# Revit family: Lighting_Ceiling-Mounted_Nordlux_Kaito-dim-LED
name_source: partatom
category: Lighting Fixtures
revit_build: Autodesk Revit 2018 (Build: 20170223_1515(x64)
units: mm (PartAtom-declared; Revit-internal decimal feet)

## family parameters
Cut with Voids When Loaded = No
Host = Face
Light Source = No
OmniClass Number = 23.35.47.11
OmniClass Title = Lighting Fixtures
Part Type = Normal
Room Calculation Point = No
Round Connector Dimension = Use Diameter
Shared = No

## types (2) — shared parameters
Apparent Load = 13 VA
BIMobject category = Ceiling Mounted
Beam angle = 109.70°
CQS = 81.7
CRI / Ra = 82.6
Default Elevation = 1219 mm
Description = Kaito Dim by Danish designer Bønnelycke MDD is carried out in a round, modern design.
Design country = Denmark
Edition number = 1
Flicker frequency = 100 Hz
IFC Classification = Light Fixture
Installation instructions = https://asset.productmarketingcloud.com
Lens material = Nordlux  - Glass  - Milky glass
Manufacturer = Nordlux
Manufacturer country = China
Manufacturer name = Nordlux
Material main = Metal
Material secondary = Plastic
Model = Kaito dim LED
NominalVoltage = 230 V
OmniClass Code = 23-35 47 11
OmniClass Description = Lighting Fixtures
Peak [cd] = 421
Power factor = 0.98
Product Guid = cbcd9ad2-4ca1-4ea0-9af8-c03f0f98357b
Product SKU = Kaito-dim-LED
Product data url = https://bimobject.com
Product family = Lighting
Product group = Ceiling
Product name = Kaito dim LED
Product url = https://nordlux.com
QR code = https://bimobject.com
TM30 Rf = 84.4
TM30 Rg = 94.9
URL = www.nordlux.com
Weight Net (Kg) = 1,1
Youtube clip = https://www.youtube.com

## per-type parameters (varying)
| type | Body material | EANNumber | Shade material |
| ART - (2220506001) Finish colour - (White) | Nordlux  - Metal  - White | 2220506001 | Nordlux  - Metal  - White |
| ART - (2220506010) Finish colour - (Grey) | Nordlux  - Metal  - Grey | 2220506010 | Nordlux  - Metal  - Grey |

## geometry (parser evidence)
native form markers: Sweep x10
no freeform markers — native parametric forms only
